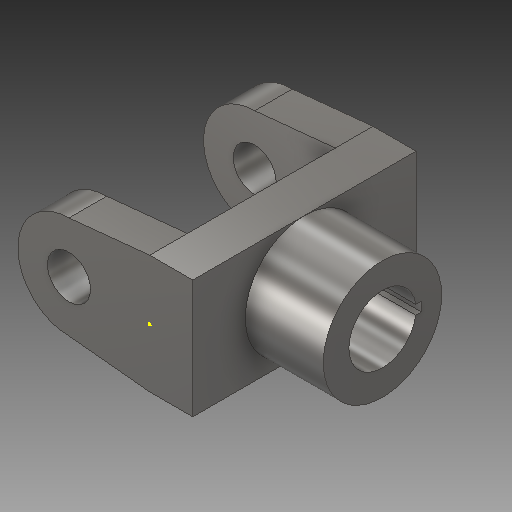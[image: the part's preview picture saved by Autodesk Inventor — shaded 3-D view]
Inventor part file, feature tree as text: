
AUTODESK INVENTOR PART (.ipt)
format: ipt  version: 2018 (Build 220112000, 112)  size: 198,144 bytes
history: native  units: mm
features: sketch x6, extrude x5
ambient origin geometry x8: Origin, YZ Plane, XZ Plane, XY Plane, X Axis, Y Axis, Z Axis, Center Point
bodies: Solid1 (feature_tree)
feature tree (11):
  extrude  "Extrusion1"  Depth=88.0mm
  extrude  "Extrusion2"  Depth=88.0mm
  extrude  "Extrusion3"  Depth=4.0mm
  sketch  "Sketch4"  dims[d7=3.5mm d8=58.0mm d9=0.0mm]
  extrude  "Extrusion4"  Depth=58.0mm TaperAngle=0.0deg
  extrude  "Extrusion5"  Depth=28.0mm
  sketch  "Sketch1"  dims[d0=166.0mm d1=88.0mm]
  sketch  "Sketch2"  dims[d2=32.0mm d3=0.0mm d4=88.0mm]
  sketch  "Sketch3"  dims[d5=50.0mm d6=4.0mm]
  sketch  "Sketch5"  dims[d10=28.0mm d11=28.0mm]
  sketch  "Sketch6"  dims[d12=98.0mm d13=0.0mm d14=76.0mm d15=98.0mm d16=0.0mm d17=32.0mm d18=98.0mm d19=0.0mm]
